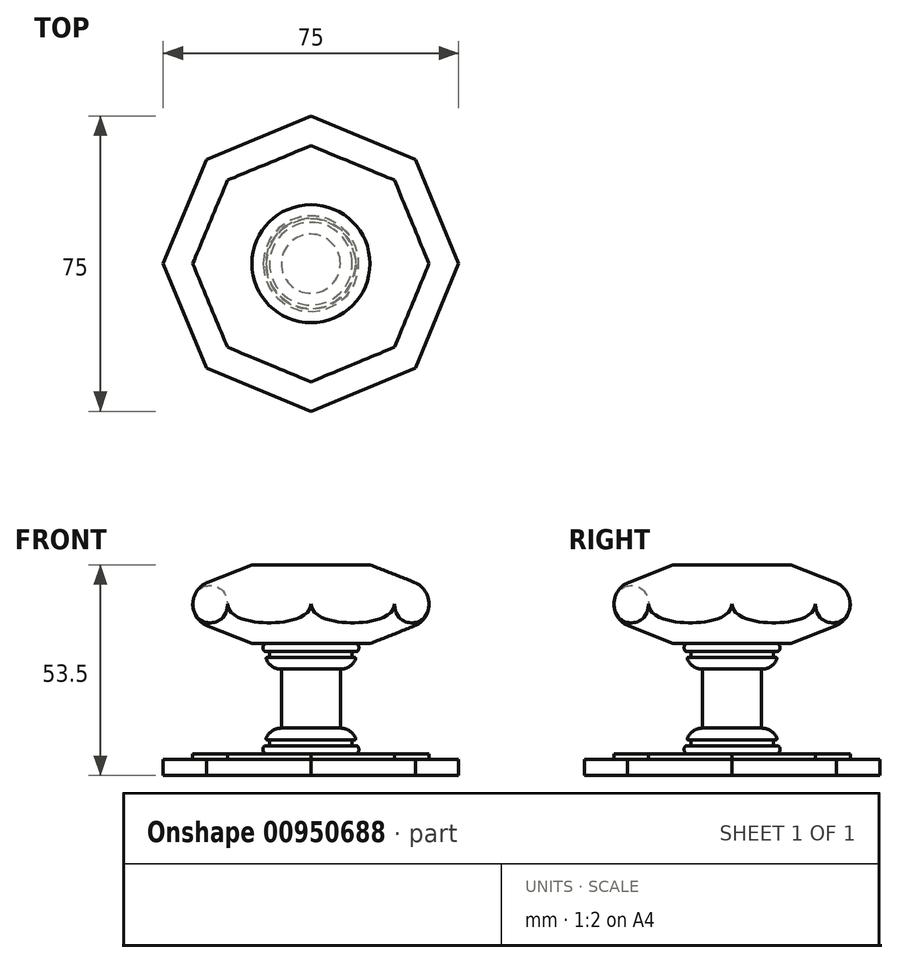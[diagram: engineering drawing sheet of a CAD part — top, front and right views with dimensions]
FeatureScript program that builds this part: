
annotation { "Feature Type Name" : "Feature", "Feature Type Description" : "" }
export const myFeature = defineFeature(function(context is Context, id is Id, definition is map)
    precondition{}
    {
        {
            var Q0;
            Q0=qCreatedBy(makeId("Top.planeOp"),FACE);
            var sketch = newSketch(context, id + "F0", { "sketchPlane" : qUnion([Q0])});
            skCircle(sketch, "E0.cCircle", {"center": v(0, 0) * mm, "radius": 37.5 * mm, "construction": true});
            skLineSegment(sketch, "E0.0", {"start": v(37.5, 0) * mm, "end": v(26.52, -26.52) * mm});
            skLineSegment(sketch, "E0.1", {"start": v(26.52, -26.52) * mm, "end": v(0, -37.5) * mm});
            skLineSegment(sketch, "E0.2", {"start": v(0, -37.5) * mm, "end": v(-26.52, -26.52) * mm});
            skLineSegment(sketch, "E0.3", {"start": v(-26.52, -26.52) * mm, "end": v(-37.5, 0) * mm});
            skLineSegment(sketch, "E0.4", {"start": v(-37.5, 0) * mm, "end": v(-26.52, 26.52) * mm});
            skLineSegment(sketch, "E0.5", {"start": v(-26.52, 26.52) * mm, "end": v(0, 37.5) * mm});
            skLineSegment(sketch, "E0.6", {"start": v(0, 37.5) * mm, "end": v(26.52, 26.52) * mm});
            skLineSegment(sketch, "E0.7", {"start": v(26.52, 26.52) * mm, "end": v(37.5, 0) * mm});
            skSolve(sketch);
        }
        {
            var Q0;
            Q0=makeQuery(id+"F0.imprint","IMPRINT",FACE,{"disambiguationData":[TD([[makeQuery(id+"F0.imprint","IMPRINT",EDGE,{"derivedFrom":sQuery(id+"F0.wireOp",EDGE,"E0.0")}),-1.0]])]});
            extrude(context, id + "F1", {"entities" : qUnion([Q0]), "depth" : 4 * mm, "offsetDistance" : 25 * mm});
        }
        {
            var Q0;
            Q0=makeQuery(id+"F1.opExtrude","CAP_FACE",FACE,{"disambiguationData":[OSD([sQuery(id+"F0.wireOp",EDGE,"E0.0"),sQuery(id+"F0.wireOp",EDGE,"E0.1"),sQuery(id+"F0.wireOp",EDGE,"E0.2"),sQuery(id+"F0.wireOp",EDGE,"E0.3"),sQuery(id+"F0.wireOp",EDGE,"E0.4"),sQuery(id+"F0.wireOp",EDGE,"E0.5"),sQuery(id+"F0.wireOp",EDGE,"E0.6"),sQuery(id+"F0.wireOp",EDGE,"E0.7")])],"isStart":false});
            var sketch = newSketch(context, id + "F2", { "sketchPlane" : qUnion([Q0])});
            skCircle(sketch, "E1.cCircle", {"center": v(0, 0) * mm, "radius": 30 * mm, "construction": true});
            skLineSegment(sketch, "E1.0", {"start": v(30, 0) * mm, "end": v(21.21, -21.21) * mm});
            skLineSegment(sketch, "E1.1", {"start": v(21.21, -21.21) * mm, "end": v(0, -30) * mm});
            skLineSegment(sketch, "E1.2", {"start": v(0, -30) * mm, "end": v(-21.21, -21.21) * mm});
            skLineSegment(sketch, "E1.3", {"start": v(-21.21, -21.21) * mm, "end": v(-30, 0) * mm});
            skLineSegment(sketch, "E1.4", {"start": v(-30, 0) * mm, "end": v(-21.21, 21.21) * mm});
            skLineSegment(sketch, "E1.5", {"start": v(-21.21, 21.21) * mm, "end": v(0, 30) * mm});
            skLineSegment(sketch, "E1.6", {"start": v(0, 30) * mm, "end": v(21.21, 21.21) * mm});
            skLineSegment(sketch, "E1.7", {"start": v(21.21, 21.21) * mm, "end": v(30, 0) * mm});
            skSolve(sketch);
        }
        {
            var Q0;
            Q0=makeQuery(id+"F2.imprint","IMPRINT",FACE,{"disambiguationData":[TD([[makeQuery(id+"F2.imprint","IMPRINT",EDGE,{"derivedFrom":sQuery(id+"F2.wireOp",EDGE,"E1.0")}),-1.0]])]});
            extrude(context, id + "F3", {"entities" : qUnion([Q0]), "operationType" : NewBodyOperationType.ADD, "depth" : 1.5 * mm, "offsetDistance" : 25 * mm});
        }
        {
            var Q0;
            Q0=qCreatedBy(makeId("Front.planeOp"),FACE);
            var sketch = newSketch(context, id + "F4", { "sketchPlane" : qUnion([Q0])});
            skLineSegment(sketch, "E2", {"start": v(0, 0) * mm, "end": v(0, 93.5) * mm, "construction": true});
            skLineSegment(sketch, "E3", {"start": v(7.5, 27) * mm, "end": v(7.5, 12) * mm});
            skLineSegment(sketch, "E4", {"start": v(11, 9) * mm, "end": v(11.1, 9) * mm});
            skLineSegment(sketch, "E5", {"start": v(10.5, 8.5) * mm, "end": v(10.5, 8) * mm});
            skLineSegment(sketch, "E6", {"start": v(11, 7.5) * mm, "end": v(11.57, 7.5) * mm});
            skLineSegment(sketch, "E7", {"start": v(11.5, 5.5) * mm, "end": v(0, 5.5) * mm});
            skArc(sketch, "E8", {"start": v(11.37, 9.4) * mm, "mid": v(9.85, 11.32) * mm, "end": v(7.5, 12) * mm});
            skArc(sketch, "E9", {"start": v(11.5, 5.5) * mm, "mid": v(12.16, 6.28) * mm, "end": v(11.97, 7.3) * mm});
            skPoint(sketch, "E10.visualSharp", {"position": v(11.5, 9) * mm});
            skArc(sketch, "E10.filletArc", {"start": v(11.1, 9) * mm, "mid": v(11.34, 9.13) * mm, "end": v(11.37, 9.4) * mm});
            skPoint(sketch, "E11.visualSharp", {"position": v(10.5, 9) * mm});
            skArc(sketch, "E11.filletArc", {"start": v(11, 9) * mm, "mid": v(10.65, 8.85) * mm, "end": v(10.5, 8.5) * mm});
            skPoint(sketch, "E12.visualSharp", {"position": v(10.5, 7.5) * mm});
            skArc(sketch, "E12.filletArc", {"start": v(10.5, 8) * mm, "mid": v(10.65, 7.65) * mm, "end": v(11, 7.5) * mm});
            skLineSegment(sketch, "E13", {"start": v(7.5, 19.5) * mm, "end": v(0, 19.5) * mm, "construction": true});
            skLineSegment(sketch, "E14.MirrorCS", {"start": v(11.5, 33.5) * mm, "end": v(0, 33.5) * mm});
            skLineSegment(sketch, "E15.MirrorCS", {"start": v(10.5, 30.5) * mm, "end": v(10.5, 31) * mm});
            skArc(sketch, "E16.MirrorCS", {"start": v(11, 30) * mm, "mid": v(10.65, 30.15) * mm, "end": v(10.5, 30.5) * mm});
            skArc(sketch, "E17.MirrorCS", {"start": v(11.1, 30) * mm, "mid": v(11.34, 29.87) * mm, "end": v(11.37, 29.6) * mm});
            skLineSegment(sketch, "E18.MirrorCS", {"start": v(11, 31.5) * mm, "end": v(11.57, 31.5) * mm});
            skLineSegment(sketch, "E19.MirrorCS", {"start": v(11, 30) * mm, "end": v(11.1, 30) * mm});
            skArc(sketch, "E20.MirrorCS", {"start": v(10.5, 31) * mm, "mid": v(10.65, 31.35) * mm, "end": v(11, 31.5) * mm});
            skArc(sketch, "E21.MirrorCS", {"start": v(11.5, 33.5) * mm, "mid": v(12.16, 32.72) * mm, "end": v(11.97, 31.7) * mm});
            skArc(sketch, "E22.MirrorCS", {"start": v(11.37, 29.6) * mm, "mid": v(9.85, 27.68) * mm, "end": v(7.5, 27) * mm});
            skPoint(sketch, "E23.MirrorP", {"position": v(10.5, 30) * mm});
            skPoint(sketch, "E24.MirrorP", {"position": v(11.5, 30) * mm});
            skPoint(sketch, "E25.MirrorP", {"position": v(10.5, 31.5) * mm});
            skLineSegment(sketch, "E26", {"start": v(0, 5.5) * mm, "end": v(0, 33.5) * mm});
            skPoint(sketch, "E27.visualSharp", {"position": v(11.78, 7.5) * mm});
            skArc(sketch, "E27.filletArc", {"start": v(11.97, 7.3) * mm, "mid": v(11.8, 7.45) * mm, "end": v(11.57, 7.5) * mm});
            skPoint(sketch, "E28.visualSharp", {"position": v(11.78, 31.5) * mm});
            skArc(sketch, "E28.filletArc", {"start": v(11.57, 31.5) * mm, "mid": v(11.8, 31.55) * mm, "end": v(11.97, 31.7) * mm});
            skSolve(sketch);
        }
        {
            var Q0;
            Q0=makeQuery(id+"F4.imprint","IMPRINT",FACE,{"disambiguationData":[TD([[makeQuery(id+"F4.imprint","IMPRINT",EDGE,{"derivedFrom":sQuery(id+"F4.wireOp",EDGE,"E3")}),-1.0]])]});
            var Q1;
            Q1=sQuery(id+"F4.wireOp",EDGE,"E2");
            revolve(context, id + "F5", {"operationType" : NewBodyOperationType.ADD, "surfaceOperationType" : NewSurfaceOperationType.NEW, "entities" : qUnion([Q0]), "axis" : qUnion([Q1]), "revolveType" : RevolveType.FULL});
        }
        {
            var Q0;
            Q0=makeQuery(id+"F5.opRevolve","SWEPT_FACE",FACE,{"disambiguationData":[OSD([sQuery(id+"F4.wireOp",EDGE,"E14.MirrorCS")])]});
            cPlane(context, id + "F6", {"entities" : qUnion([Q0]), "cplaneType" : CPlaneType.OFFSET, "offset" : 20 * mm, "width" : 150 * mm, "height" : 150 * mm});
        }
        {
            var Q0;
            Q0=qCreatedBy(id+"F6.planeOp",FACE);
            var sketch = newSketch(context, id + "F7", { "sketchPlane" : qUnion([Q0])});
            skCircle(sketch, "E29.cCircle", {"center": v(0, 0) * mm, "radius": 30 * mm, "construction": true});
            skLineSegment(sketch, "E29.0", {"start": v(30, 0) * mm, "end": v(21.21, -21.21) * mm});
            skLineSegment(sketch, "E29.1", {"start": v(21.21, -21.21) * mm, "end": v(0, -30) * mm});
            skLineSegment(sketch, "E29.2", {"start": v(0, -30) * mm, "end": v(-21.21, -21.21) * mm});
            skLineSegment(sketch, "E29.3", {"start": v(-21.21, -21.21) * mm, "end": v(-30, 0) * mm});
            skLineSegment(sketch, "E29.4", {"start": v(-30, 0) * mm, "end": v(-21.21, 21.21) * mm});
            skLineSegment(sketch, "E29.5", {"start": v(-21.21, 21.21) * mm, "end": v(0, 30) * mm});
            skLineSegment(sketch, "E29.6", {"start": v(0, 30) * mm, "end": v(21.21, 21.21) * mm});
            skLineSegment(sketch, "E29.7", {"start": v(21.21, 21.21) * mm, "end": v(30, 0) * mm});
            skSolve(sketch);
        }
        {
            var Q0;
            Q0=qSketchRegion(id+"F7",true);
            var Q1;
            Q1=makeQuery(id+"F5.opRevolve","SWEPT_FACE",FACE,{"disambiguationData":[OSD([sQuery(id+"F4.wireOp",EDGE,"E14.MirrorCS")])]});
            extrude(context, id + "F8", {"entities" : qUnion([Q0]), "operationType" : NewBodyOperationType.ADD, "endBound" : BoundingType.UP_TO_SURFACE, "oppositeDirection" : true, "depth" : 25 * mm, "endBoundEntityFace" : qUnion([Q1]), "offsetDistance" : 25 * mm});
        }
        {
            var Q0;
            Q0=qCreatedBy(makeId("Front.planeOp"),FACE);
            var sketch = newSketch(context, id + "F9", { "sketchPlane" : qUnion([Q0])});
            skLineSegment(sketch, "E30", {"start": v(0, 0) * mm, "end": v(0, 62.18) * mm, "construction": true});
            skLineSegment(sketch, "E31", {"start": v(30, 43.5) * mm, "end": v(-30, 43.5) * mm, "construction": true});
            skArc(sketch, "E32", {"start": v(26.2, 37.92) * mm, "mid": v(30, 43.5) * mm, "end": v(26.2, 49.08) * mm});
            skLineSegment(sketch, "E33", {"start": v(26.2, 49.08) * mm, "end": v(15, 53.5) * mm});
            skLineSegment(sketch, "E34", {"start": v(26.2, 37.92) * mm, "end": v(15, 33.5) * mm});
            skLineSegment(sketch, "E35", {"start": v(15, 53.5) * mm, "end": v(37.5, 53.5) * mm});
            skLineSegment(sketch, "E36", {"start": v(37.5, 53.5) * mm, "end": v(37.5, 33.5) * mm});
            skLineSegment(sketch, "E37", {"start": v(37.5, 33.5) * mm, "end": v(15, 33.5) * mm});
            skSolve(sketch);
        }
        {
            var Q0;
            Q0=qSketchRegion(id+"F9",true);
            var Q1;
            Q1=sQuery(id+"F9.wireOp",EDGE,"E30");
            revolve(context, id + "F10", {"operationType" : NewBodyOperationType.REMOVE, "surfaceOperationType" : NewSurfaceOperationType.NEW, "entities" : qUnion([Q0]), "axis" : qUnion([Q1]), "revolveType" : RevolveType.FULL, "oppositeDirection" : true});
        }
    });
